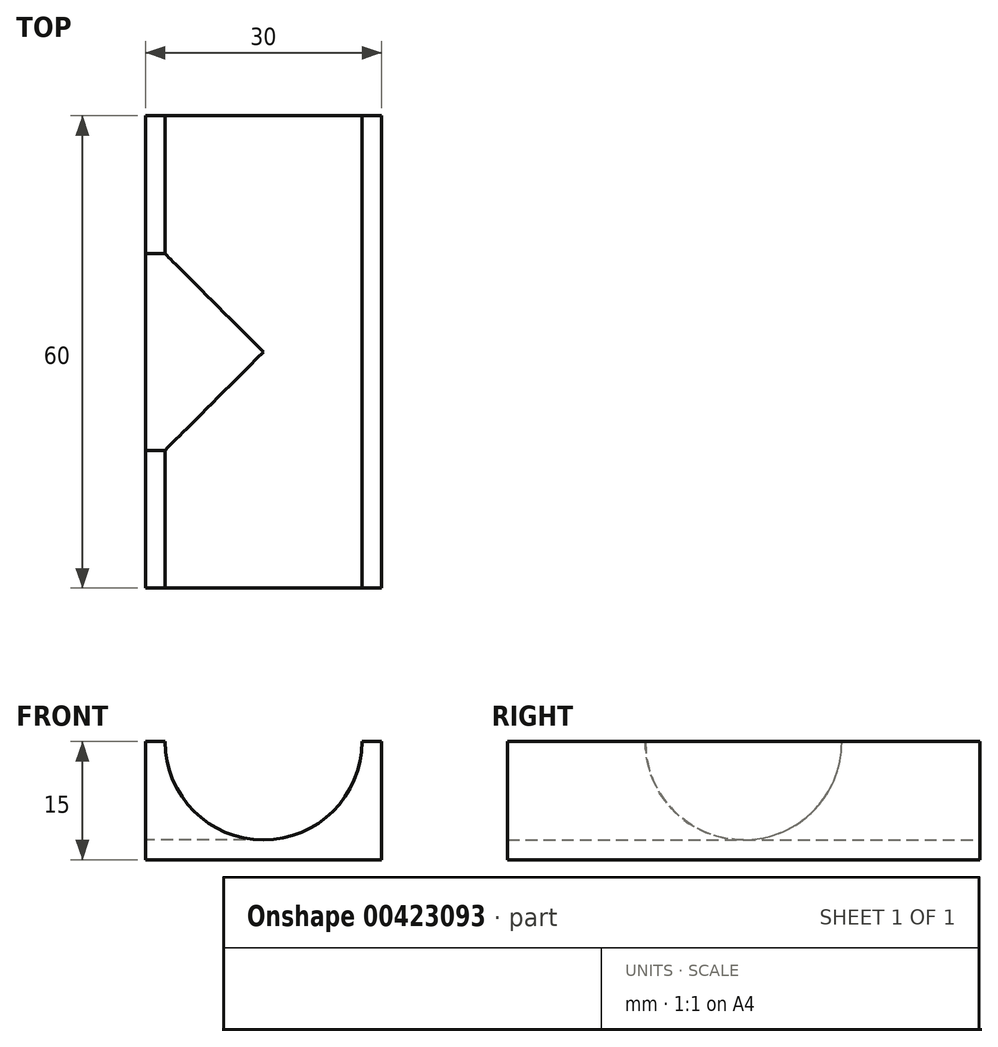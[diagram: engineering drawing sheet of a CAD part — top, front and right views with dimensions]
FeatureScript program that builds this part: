
annotation { "Feature Type Name" : "Feature", "Feature Type Description" : "" }
export const myFeature = defineFeature(function(context is Context, id is Id, definition is map)
    precondition{}
    {
        {
            var Q0;
            Q0=qCreatedBy(makeId("Front.planeOp"),FACE);
            var sketch = newSketch(context, id + "F0", { "sketchPlane" : qUnion([Q0])});
            skLineSegment(sketch, "E0", {"start": v(0, 0) * mm, "end": v(30, 0) * mm});
            skLineSegment(sketch, "E1", {"start": v(30, 0) * mm, "end": v(30, 15) * mm});
            skLineSegment(sketch, "E2", {"start": v(30, 15) * mm, "end": v(27.5, 15) * mm});
            skLineSegment(sketch, "E3", {"start": v(0, 15) * mm, "end": v(2.5, 15) * mm});
            skArc(sketch, "E4", {"start": v(2.5, 15) * mm, "mid": v(15, 2.5) * mm, "end": v(27.5, 15) * mm});
            skLineSegment(sketch, "E5", {"start": v(0, 0) * mm, "end": v(0, 15) * mm});
            skSolve(sketch);
        }
        {
            var Q0;
            Q0 = qSketchRegion(id + "F0", true);
            extrude(context, id + "F1", {"entities" : qUnion([Q0]), "endBound" : BoundingType.SYMMETRIC, "depth" : 60 * mm});
        }
        {
            var Q0;
            Q0=qCreatedBy(makeId("Right.planeOp"),FACE);
            var sketch = newSketch(context, id + "F2", { "sketchPlane" : qUnion([Q0])});
            skCircle(sketch, "E6", {"center": v(0, 15) * mm, "radius": 12.5 * mm});
            skSolve(sketch);
        }
        {
            var Q0;
            Q0 = qSketchRegion(id + "F2", true);
            extrude(context, id + "F3", {"entities" : qUnion([Q0]), "operationType" : NewBodyOperationType.REMOVE, "depth" : 15 * mm});
        }
    });
